# Revit family: LTR-6SQA
name_source: partatom
category: Lighting Fixtures
units: mm (PartAtom-declared; Revit-internal decimal feet)

## family parameters
Cut with Voids When Loaded = No
Host = Face
Light Source = Yes
OmniClass Number = 23.80.70.11.14.11
OmniClass Title = Downlights
Part Type = Normal
Room Calculation Point = No
Round Connector Dimension = Use Diameter
Shared = Yes

## types (1)
- LTR-6SQA
    Apparent Load = 0 VA
    Assembly Code = D5020200
    Color Filter = 16777215
    Default Elevation = 48 "
    Description = LITEISTRY™ 6inch Square Adjustable
    Dimming Lamp Color Temperature Shift = <None>
    Emit Shape Visible in Rendering = No
    Emit from Rectangle Length = 6 "
    Emit from Rectangle Width = 6 "
    Features = • 6inch architectural LED adjustable accent delivering 600–3500 lm • Four field interchangeable beam distributions from 15° to 45° • Translating center beam optic allows 0–35° vertical tilt, 362° horizontal rotation • Accommodates up to two lens media including hexcell louver and linear spread options • Variety of dimming protocol options including 0-10V, DALI, DMX, Lutron Forward Phase and EcoSystem • NX Distributed Intelligence™ wired and wireless controls capability available
    Glass = White Glass
    Hardware Finish = Steel
    Lamp = LED
    Load Classification = Lighting
    Manufacturer = Litecontrol
    Model = LTR-6SQA
    Photometric Notes = More IES files download on Photometric Web Link
    Photometric Web File = generic.ies
    Power Factor = 1
    Tilt Angle = -90.00°
    URL = https://www.currentlighting.com
    Voltage = 120 V
    Warranty = 5Years limited warranty
    Wattage Comments = 8-52

## geometry (parser evidence)
native form markers: Blend x1, Sweep x1
no freeform markers — native parametric forms only
